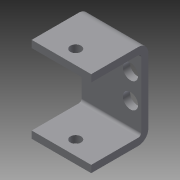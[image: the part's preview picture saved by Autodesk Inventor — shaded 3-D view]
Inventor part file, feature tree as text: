
AUTODESK INVENTOR PART (.ipt)
format: ipt  version: 2013 (Build 170138000, 138)  size: 134,144 bytes
history: native  units: in
note: dims shown in document units (in); Inventor stores cm internally (conversion verified against a paired STEP export)
features: sketch x5, sheet_metal_op x4, other x3, reference x2, extrude x1
ambient origin geometry x8: Origin, YZ Plane, XZ Plane, XY Plane, X Axis, Y Axis, Z Axis, Center Point
bodies: Solid1 (feature_tree)
feature tree (15):
  sheet_metal_op  "Face1"
  sheet_metal_op  "Flange1"
  extrude  "Extrusion1"  Depth=1.15in
  sketch  "Sketch8"  dims[d9=0.25in d10=0.125in d11=1.0in d12=90.0deg d13=0.05in d14=0.5in d15=0.125in d16=0.125in d17=0.25in d18=0.1875in d19=2999.0in d20=0.0in d21=0.575in d26=0.125in d27=0.0in]
  sketch  "Sketch1"  dims[d4=0.5788in d5=1.15in]
  other  "Plate1"
  sketch  "Sketch2"  dims[d6=0.125in]
  other  "Plate2"
  sheet_metal_op  "Bend1"
  sheet_metal_op  "Corner1"
  sketch  "Sketch3"  dims[d7=0.125in]
  sketch  "Sketch7"  dims[d8=0.0625in]
  reference  "Reference4"
  reference  "Reference5"
  other  "Cut3"
